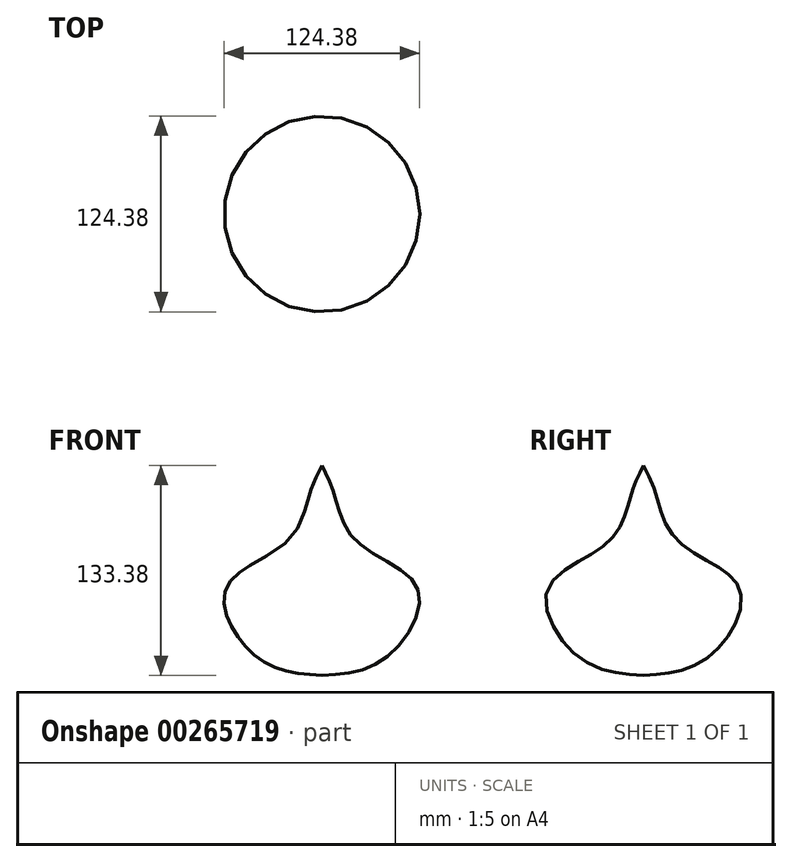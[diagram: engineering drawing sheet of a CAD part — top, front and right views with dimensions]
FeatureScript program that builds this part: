
annotation { "Feature Type Name" : "Feature", "Feature Type Description" : "" }
export const myFeature = defineFeature(function(context is Context, id is Id, definition is map)
    precondition{}
    {
        {
            var Q0;
            Q0=qCreatedBy(makeId("Front.planeOp"),FACE);
            var sketch = newSketch(context, id + "F0", { "sketchPlane" : qUnion([Q0])});
            skFitSpline(sketch, "E0", {"points": [v(0, -63.7) * mm, v(40.91, -52.3) * mm, v(61, -8.84) * mm, v(22.03, 21.43) * mm, v(7.64, 52) * mm, v(0, 69.69) * mm], "startDerivative": vector(199.6, 12.35) * mm, "endDerivative": vector(-57.05, 111.7) * mm});
            skLineSegment(sketch, "E1", {"start": v(0, 69.69) * mm, "end": v(0, -63.7) * mm});
            skSolve(sketch);
        }
        {
            var Q0;
            Q0=makeQuery(id+"F0.imprint","IMPRINT",FACE,{"disambiguationData":[TD([[makeQuery(id+"F0.imprint","IMPRINT",EDGE,{"derivedFrom":sQuery(id+"F0.wireOp",EDGE,"E0")}),1.0]])]});
            var Q1;
            Q1=sQuery(id+"F0.wireOp",EDGE,"E1");
            revolve(context, id + "F1", {"entities" : qUnion([Q0]), "axis" : qUnion([Q1]), "revolveType" : RevolveType.FULL});
        }
    });
